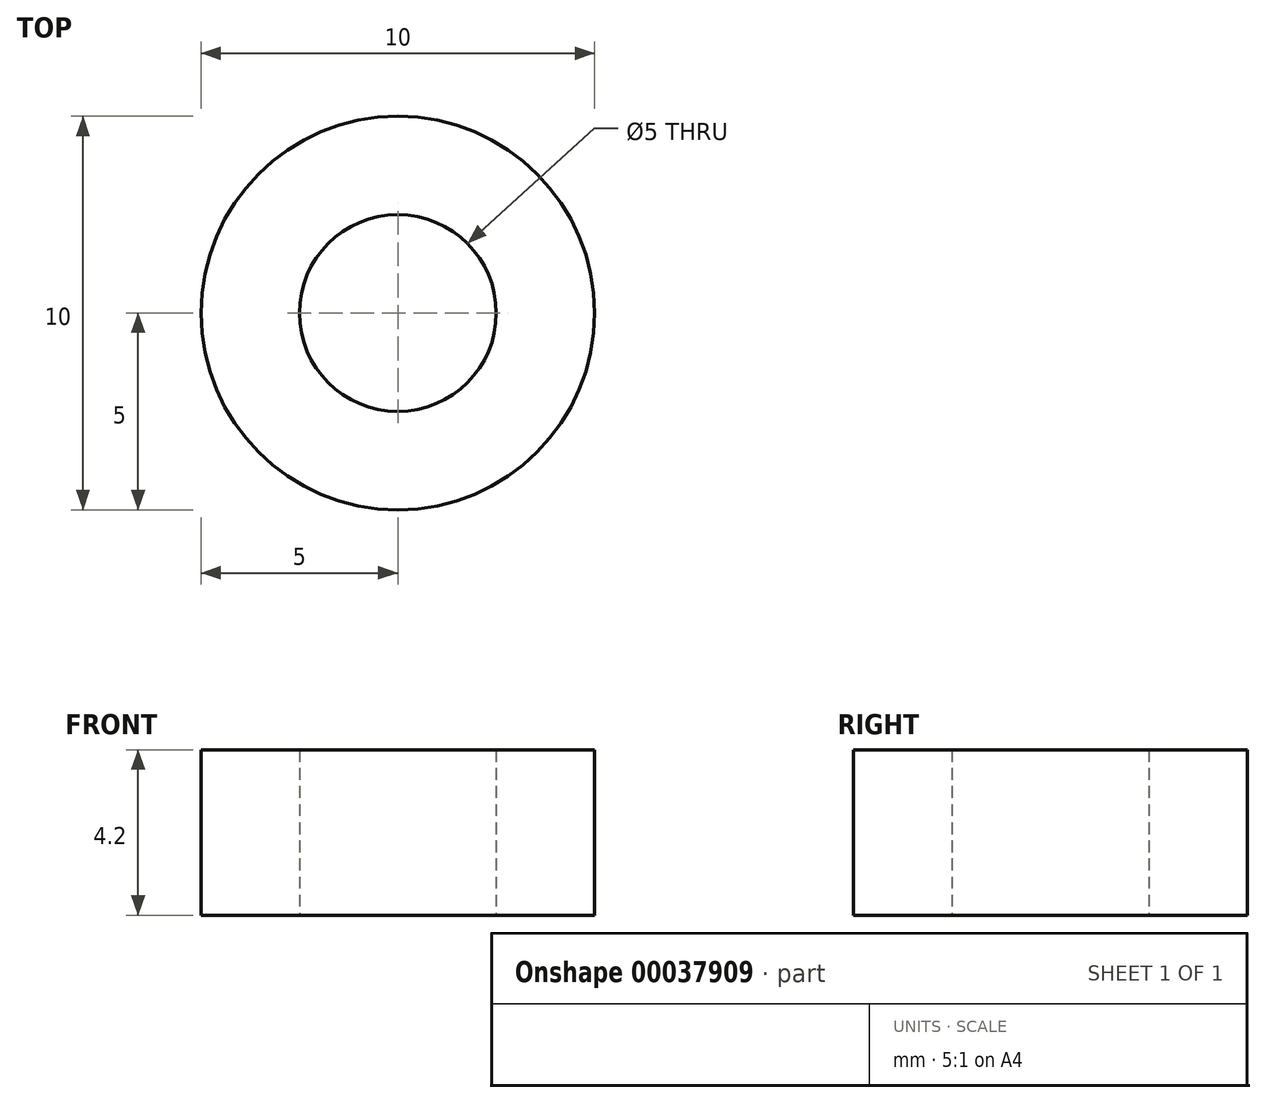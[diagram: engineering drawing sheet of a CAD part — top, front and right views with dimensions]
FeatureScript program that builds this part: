
annotation { "Feature Type Name" : "Feature", "Feature Type Description" : "" }
export const myFeature = defineFeature(function(context is Context, id is Id, definition is map)
    precondition{}
    {
        {
            var Q0;
            Q0=qCreatedBy(makeId("Top.planeOp"),FACE);
            var sketch = newSketch(context, id + "F0", { "sketchPlane" : qUnion([Q0])});
            skCircle(sketch, "E0", {"center": v(0, 0) * mm, "radius": 2.5 * mm});
            skCircle(sketch, "E1", {"center": v(0, 0) * mm, "radius": 5 * mm});
            skSolve(sketch);
        }
        {
            var Q0;
            Q0 = qSketchRegion(id + "F0", true);
            extrude(context, id + "F1", {"entities" : qUnion([Q0]), "depth" : 4.2 * mm});
        }
    });
